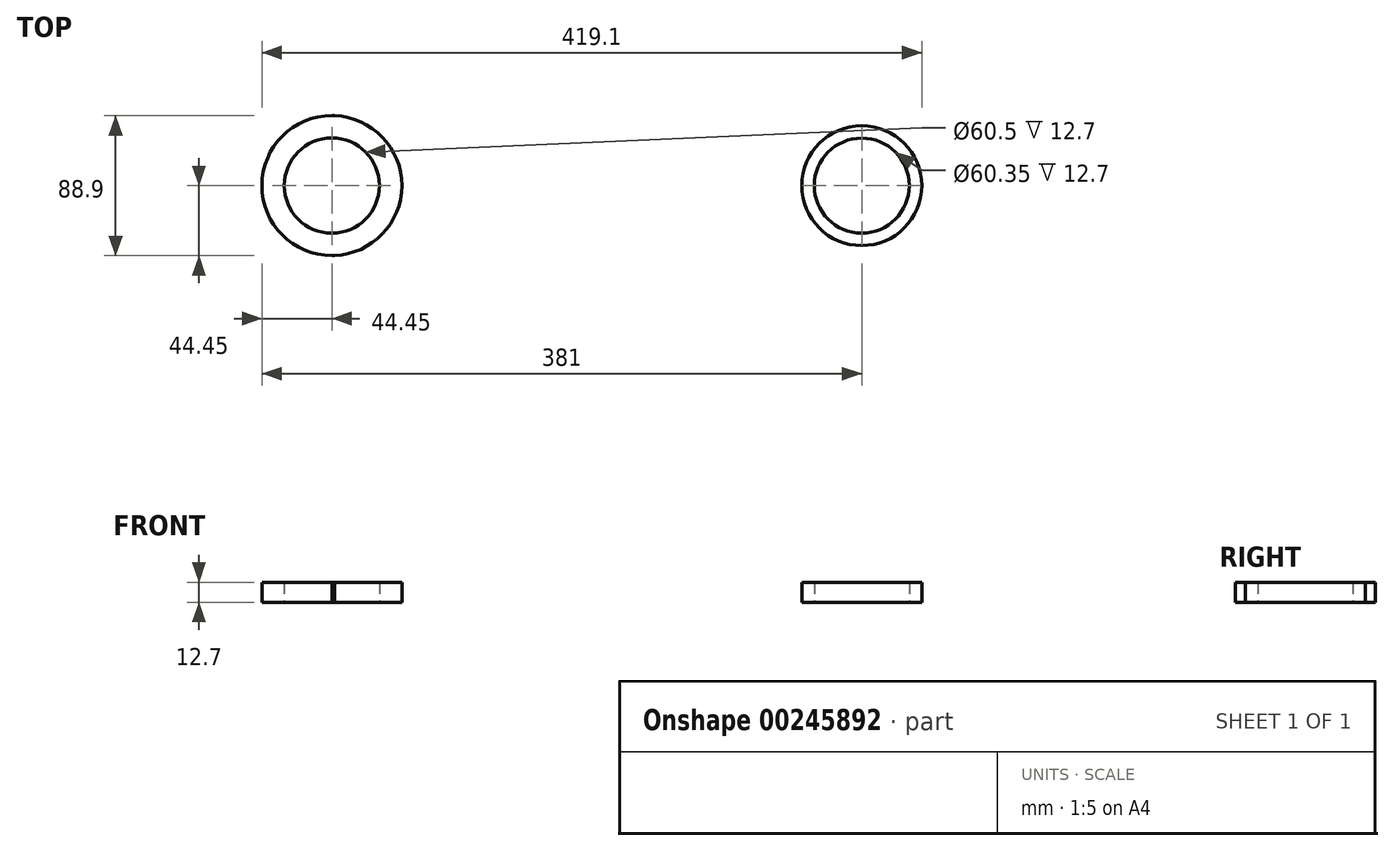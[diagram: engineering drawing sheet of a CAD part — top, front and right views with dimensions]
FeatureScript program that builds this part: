
annotation { "Feature Type Name" : "Feature", "Feature Type Description" : "" }
export const myFeature = defineFeature(function(context is Context, id is Id, definition is map)
    precondition{}
    {
        {
            var Q0;
            Q0=qCreatedBy(makeId("Top.planeOp"),FACE);
            var sketch = newSketch(context, id + "F0", { "sketchPlane" : qUnion([Q0])});
            skCircle(sketch, "E0", {"center": v(-120.09, 0) * mm, "radius": 30.25 * mm});
            skCircle(sketch, "E1", {"center": v(-120.09, 0) * mm, "radius": 44.45 * mm});
            skCircle(sketch, "E2", {"center": v(216.46, 0) * mm, "radius": 30.18 * mm});
            skCircle(sketch, "E3", {"center": v(216.46, 0) * mm, "radius": 38.1 * mm});
            skLineSegment(sketch, "E4", {"start": v(-164.54, 0) * mm, "end": v(254.56, 0) * mm, "construction": true});
            skLineSegment(sketch, "E5", {"start": v(-120.09, -44.45) * mm, "end": v(216.46, -38.1) * mm});
            skLineSegment(sketch, "E6", {"start": v(-120.09, 44.45) * mm, "end": v(216.46, 38.1) * mm});
            skLineSegment(sketch, "E7", {"start": v(-75.64, 0) * mm, "end": v(178.36, 0) * mm});
            skSolve(sketch);
        }
        {
            var Q0;
            Q0=makeQuery(id+"F0.imprint","IMPRINT",FACE,{"disambiguationData":[TD([[makeQuery(id+"F0.imprint","IMPRINT",EDGE,{"derivedFrom":sQuery(id+"F0.wireOp",EDGE,"E0")}),-1.0]])]});
            var Q1;
            {var subQ0=sQuery(id+"F0.wireOp",EDGE,"E5");Q1=makeQuery(id+"F0.imprint","IMPRINT",FACE,{"disambiguationData":[TD([[makeQuery(id+"F0.imprint","IMPRINT",EDGE,{"derivedFrom":subQ0}),1.0]])]});}
            var Q2;
            Q2=makeQuery(id+"F0.imprint","IMPRINT",FACE,{"disambiguationData":[TD([[makeQuery(id+"F0.imprint","IMPRINT",EDGE,{"derivedFrom":sQuery(id+"F0.wireOp",EDGE,"E2")}),-1.0]])]});
            extrude(context, id + "F1", {"entities" : qUnion([Q0, Q1, Q2]), "depth" : 12.7 * mm});
        }
    });
